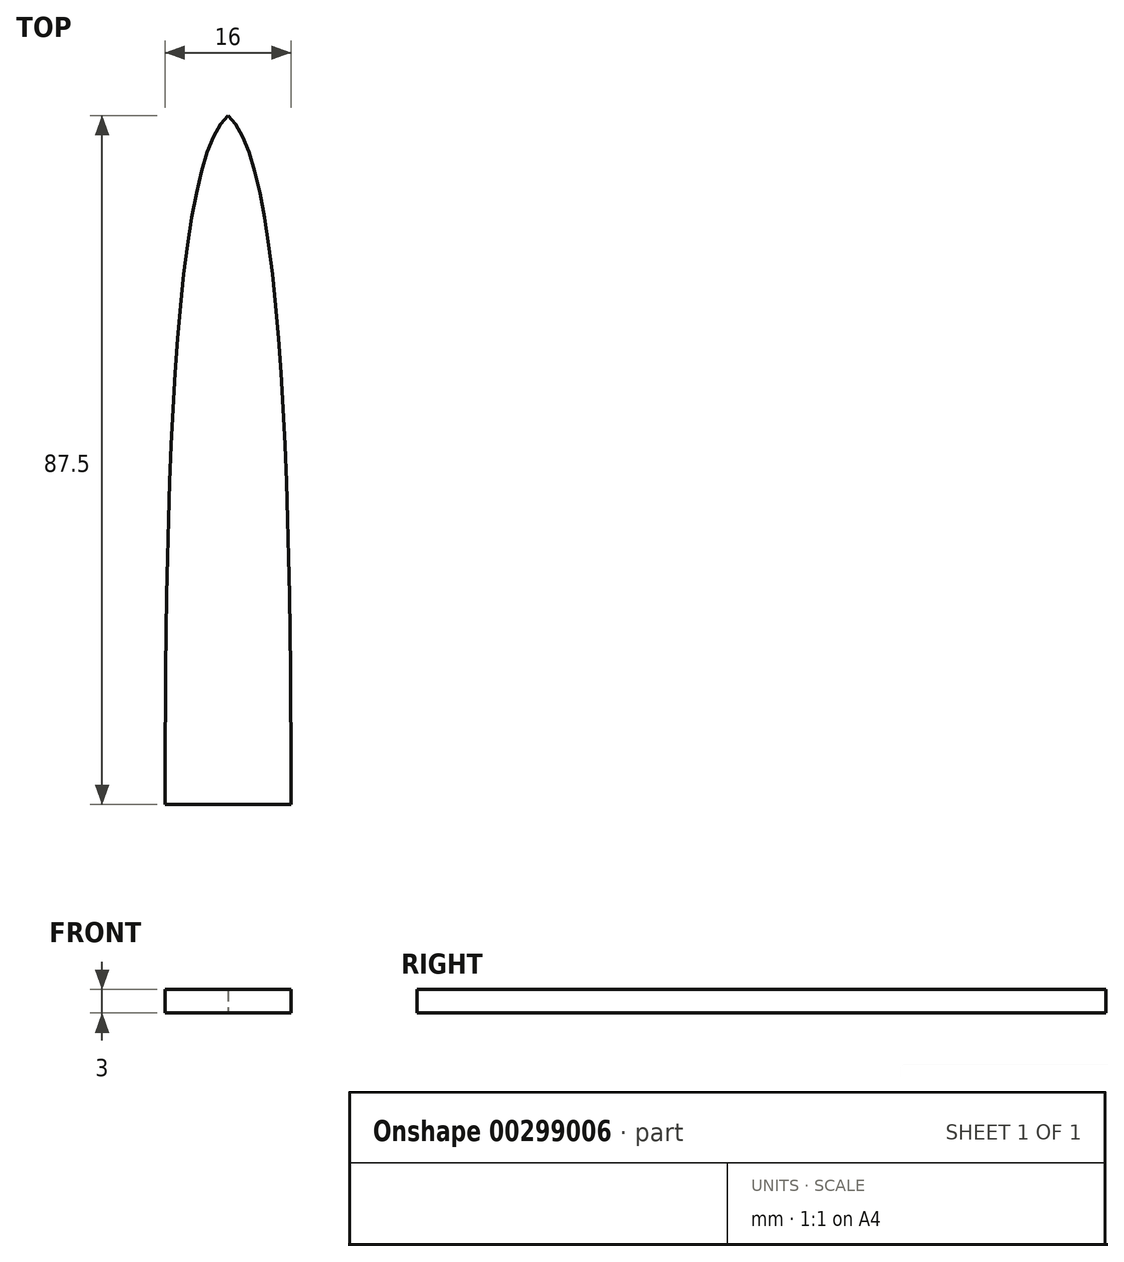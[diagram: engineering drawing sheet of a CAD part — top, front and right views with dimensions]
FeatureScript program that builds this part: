
annotation { "Feature Type Name" : "Feature", "Feature Type Description" : "" }
export const myFeature = defineFeature(function(context is Context, id is Id, definition is map)
    precondition{}
    {
        {
            var Q0;
            Q0=qCreatedBy(makeId("Top.planeOp"),FACE);
            var sketch = newSketch(context, id + "F0", { "sketchPlane" : qUnion([Q0])});
            skLineSegment(sketch, "E0", {"start": v(0, 0) * mm, "end": v(8, 0) * mm});
            skLineSegment(sketch, "E1", {"start": v(0, 0) * mm, "end": v(0, 87.5) * mm, "construction": true});
            skFitSpline(sketch, "E2", {"points": [v(0, 87.5) * mm, v(8, 0) * mm], "startDerivative": vector(22.98, -19.28) * mm, "endDerivative": vector(0, -90) * mm});
            skLineSegment(sketch, "E3", {"start": v(8, 0) * mm, "end": v(8, 30) * mm, "construction": true});
            skLineSegment(sketch, "E4", {"start": v(0, 87.5) * mm, "end": v(7.66, 81.07) * mm, "construction": true});
            skFitSpline(sketch, "E5.MirrorCS", {"points": [v(0, 87.5) * mm, v(-8, 0) * mm], "startDerivative": vector(-22.98, -19.28) * mm, "endDerivative": vector(0, -90) * mm});
            skLineSegment(sketch, "E6.MirrorCS", {"start": v(0, 0) * mm, "end": v(-8, 0) * mm});
            skSolve(sketch);
        }
        {
            var Q0;
            Q0 = qSketchRegion(id + "F0", true);
            extrude(context, id + "F1", {"entities" : qUnion([Q0]), "depth" : 3 * mm});
        }
    });
